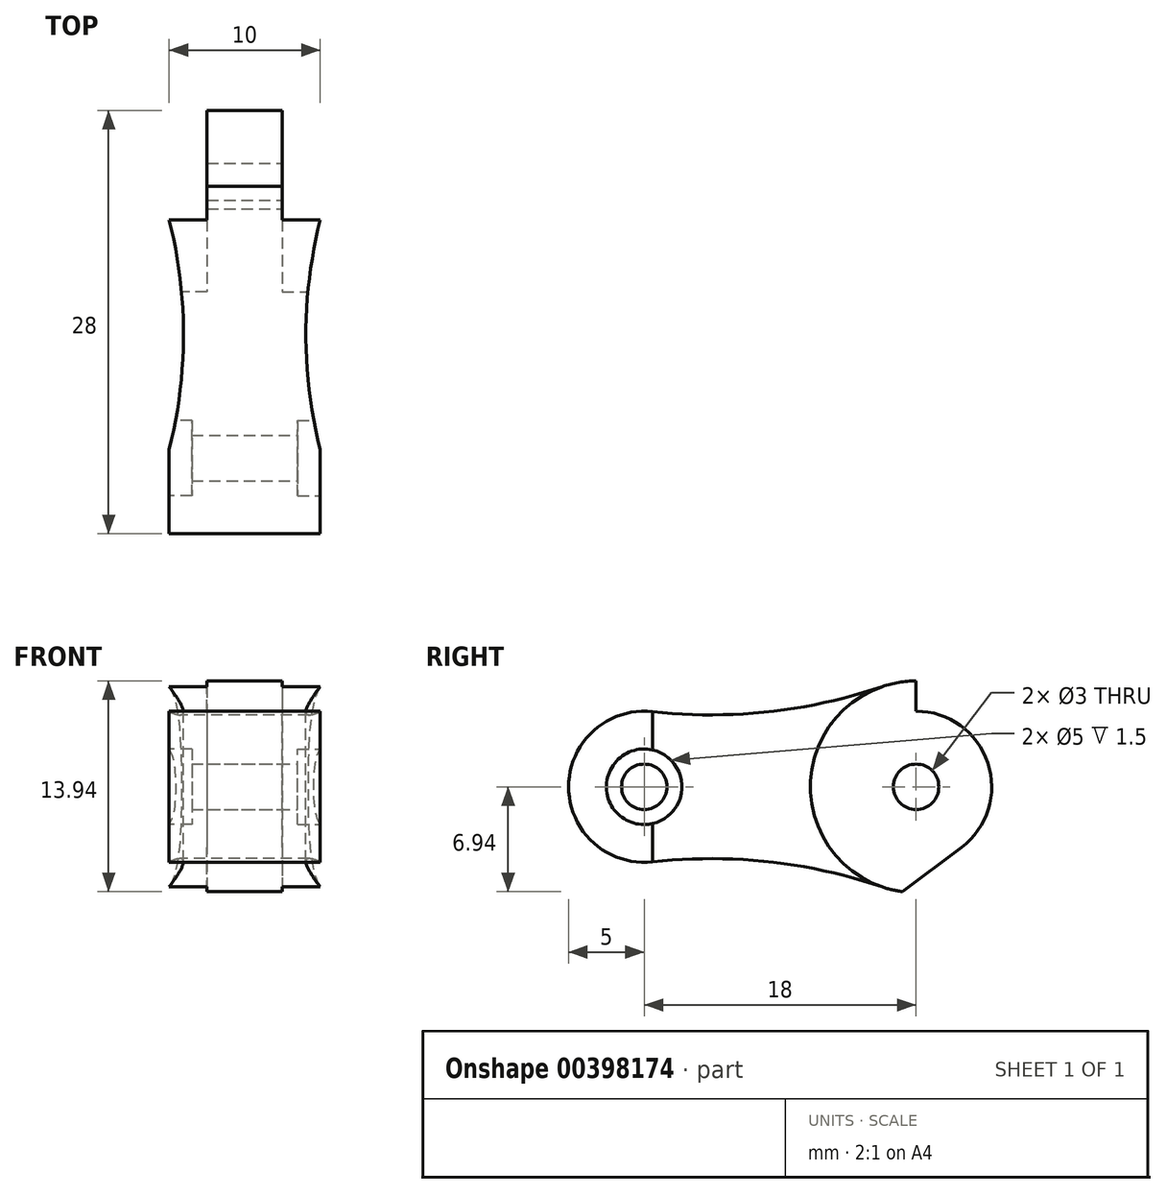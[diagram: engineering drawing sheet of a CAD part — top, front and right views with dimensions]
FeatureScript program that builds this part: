
annotation { "Feature Type Name" : "Feature", "Feature Type Description" : "" }
export const myFeature = defineFeature(function(context is Context, id is Id, definition is map)
    precondition{}
    {
        {
            var Q0;
            Q0=qCreatedBy(makeId("Right.planeOp"),FACE);
            var sketch = newSketch(context, id + "F0", { "sketchPlane" : qUnion([Q0])});
            skArc(sketch, "E0", {"start": v(0.55, 4.97) * mm, "mid": v(-5, 0) * mm, "end": v(0.55, -4.97) * mm});
            skLineSegment(sketch, "E1", {"start": v(-29.92, 0) * mm, "end": v(87.26, 0) * mm, "construction": true});
            skArc(sketch, "E2", {"start": v(15.75, -6.63) * mm, "mid": v(25, 0) * mm, "end": v(15.75, 6.63) * mm});
            skArc(sketch, "E3", {"start": v(0.55, 4.97) * mm, "mid": v(8.24, 4.96) * mm, "end": v(15.75, 6.63) * mm});
            skArc(sketch, "E4", {"start": v(15.75, -6.63) * mm, "mid": v(8.24, -4.96) * mm, "end": v(0.55, -4.97) * mm});
            skSolve(sketch);
        }
        {
            var Q0;
            Q0=qSketchRegion(id+"F0",true);
            extrude(context, id + "F1", {"entities" : qUnion([Q0]), "depth" : 2.5 * mm});
        }
        {
            var Q0;
            Q0=makeQuery(id+"F1.opExtrude","CAP_FACE",FACE,{"disambiguationData":[OSD([sQuery(id+"F0.wireOp",EDGE,"E0"),sQuery(id+"F0.wireOp",EDGE,"E2"),sQuery(id+"F0.wireOp",EDGE,"E3"),sQuery(id+"F0.wireOp",EDGE,"E4")])],"isStart":false});
            var sketch = newSketch(context, id + "F2", { "sketchPlane" : qUnion([Q0])});
            skArc(sketch, "E5.0", {"start": v(0.55, 4.97) * mm, "mid": v(8.24, 4.96) * mm, "end": v(15.75, 6.63) * mm});
            skArc(sketch, "E6.0", {"start": v(15.75, -6.63) * mm, "mid": v(25, 0) * mm, "end": v(15.75, 6.63) * mm});
            skLineSegment(sketch, "E7", {"start": v(0, 0) * mm, "end": v(34.92, 0) * mm, "construction": true});
            skPoint(sketch, "E8.orphan", {"position": v(0.55, -4.97) * mm});
            skArc(sketch, "E9.0", {"start": v(0.55, 4.97) * mm, "mid": v(-5, 0) * mm, "end": v(0.55, -4.97) * mm});
            skArc(sketch, "E10.0", {"start": v(15.75, -6.63) * mm, "mid": v(8.24, -4.96) * mm, "end": v(0.55, -4.97) * mm});
            skSolve(sketch);
        }
        {
            var Q0;
            Q0=qSketchRegion(id+"F2",true);
            extrude(context, id + "F3", {"entities" : qUnion([Q0]), "operationType" : NewBodyOperationType.ADD, "depth" : 5 * mm});
        }
        {
            var Q0;
            Q0=makeQuery(id+"F3.opExtrude","CAP_FACE",FACE,{"disambiguationData":[OSD([sQuery(id+"F2.wireOp",EDGE,"E5.0"),sQuery(id+"F2.wireOp",EDGE,"bc38228c-ca1f-41e0-8e1d-5deb207440e8.0"),sQuery(id+"F2.wireOp",EDGE,"a1095cbb-552a-4b33-82fb-9fb0068e6b7f.0"),sQuery(id+"F2.wireOp",EDGE,"E6.0"),sQuery(id+"F2.wireOp",EDGE,"kkhRfJHV-auDH-NZtS-KPEK-8B2iLmtzf0xF"),sQuery(id+"F2.wireOp",EDGE,"MWx028tx-hoiO-j3L1-AWWv-dpKiWbue3HpV"),sQuery(id+"F2.wireOp",EDGE,"JRJ70NO1-7vJe-Li3z-EIXT-plhISmGAnEbH")])],"isStart":false});
            var sketch = newSketch(context, id + "F4", { "sketchPlane" : qUnion([Q0])});
            skArc(sketch, "E11.0", {"start": v(0.55, 4.97) * mm, "mid": v(8.24, 4.96) * mm, "end": v(15.75, 6.63) * mm});
            skArc(sketch, "E12.0", {"start": v(24.57, -2.42) * mm, "mid": v(23.01, 4.89) * mm, "end": v(15.75, 6.63) * mm});
            skArc(sketch, "E13.0", {"start": v(15.75, -6.63) * mm, "mid": v(25, 0) * mm, "end": v(15.75, 6.63) * mm});
            skArc(sketch, "E14.0", {"start": v(0.55, 4.97) * mm, "mid": v(-5, 0) * mm, "end": v(0.55, -4.97) * mm});
            skArc(sketch, "E15.0", {"start": v(15.75, -6.63) * mm, "mid": v(8.24, -4.96) * mm, "end": v(0.55, -4.97) * mm});
            skSolve(sketch);
        }
        {
            var Q0;
            Q0=qSketchRegion(id+"F4",true);
            extrude(context, id + "F5", {"entities" : qUnion([Q0]), "operationType" : NewBodyOperationType.ADD, "depth" : 2.5 * mm});
        }
        {
            var Q0;
            Q0=makeQuery(id+"F5.opExtrude","CAP_FACE",FACE,{"disambiguationData":[OSD([sQuery(id+"F4.wireOp",EDGE,"b5f4364b-fbc1-4a31-856a-9d50cbaf00ff.0"),sQuery(id+"F4.wireOp",EDGE,"E11.0"),sQuery(id+"F4.wireOp",EDGE,"e0418f54-8eee-4f44-a8f3-dbf9244a5c95.0"),sQuery(id+"F4.wireOp",EDGE,"98b7fe89-a05e-4f80-a394-89aa36924708.0"),sQuery(id+"F4.wireOp",EDGE,"E12.0"),sQuery(id+"F4.wireOp",EDGE,"9f62abc7-1666-4e20-9411-6d2521d5bc1d.0")])],"isStart":false});
            var sketch = newSketch(context, id + "F6", { "sketchPlane" : qUnion([Q0])});
            skCircle(sketch, "E16", {"center": v(18, 0) * mm, "radius": 7 * mm});
            skSolve(sketch);
        }
        {
            var Q0;
            Q0=qSketchRegion(id+"F6",true);
            extrude(context, id + "F7", {"entities" : qUnion([Q0]), "operationType" : NewBodyOperationType.REMOVE, "oppositeDirection" : true, "depth" : 2.5 * mm});
        }
        {
            var Q0;
            Q0=makeQuery(id+"F1.opExtrude","CAP_FACE",FACE,{"disambiguationData":[OSD([sQuery(id+"F0.wireOp",EDGE,"E0"),sQuery(id+"F0.wireOp",EDGE,"E2"),sQuery(id+"F0.wireOp",EDGE,"E3"),sQuery(id+"F0.wireOp",EDGE,"E4")])],"isStart":true});
            var sketch = newSketch(context, id + "F8", { "sketchPlane" : qUnion([Q0])});
            skCircle(sketch, "E17", {"center": v(-18, 0) * mm, "radius": 7 * mm});
            skSolve(sketch);
        }
        {
            var Q0;
            Q0=qSketchRegion(id+"F8",true);
            extrude(context, id + "F9", {"entities" : qUnion([Q0]), "operationType" : NewBodyOperationType.REMOVE, "oppositeDirection" : true, "depth" : 2.5 * mm});
        }
        {
            var Q0;
            Q0=makeQuery(id+"F7.boolean.opBoolean","COPY",FACE,{"derivedFrom":makeQuery(id+"F7.opExtrude","CAP_FACE",FACE,{"disambiguationData":[OSD([sQuery(id+"F6.wireOp",EDGE,"E16")])],"isStart":false})});
            var sketch = newSketch(context, id + "F10", { "sketchPlane" : qUnion([Q0])});
            skArc(sketch, "E18", {"start": v(21, -4) * mm, "mid": v(22.74, 1.58) * mm, "end": v(18, 5) * mm});
            skLineSegment(sketch, "E19", {"start": v(18, 7) * mm, "end": v(18, 5) * mm});
            skArc(sketch, "E20", {"start": v(17.08, -6.94) * mm, "mid": v(24.98, -0.46) * mm, "end": v(18, 7) * mm});
            skLineSegment(sketch, "E21", {"start": v(21, -4) * mm, "end": v(17.08, -6.94) * mm});
            skSolve(sketch);
        }
        {
            var Q0;
            Q0=qSketchRegion(id+"F10",true);
            extrude(context, id + "F11", {"entities" : qUnion([Q0]), "operationType" : NewBodyOperationType.REMOVE, "endBound" : BoundingType.THROUGH_ALL, "oppositeDirection" : true, "depth" : 25 * mm});
        }
        {
            var Q0;
            Q0=makeQuery(id+"F5.opExtrude","CAP_FACE",FACE,{"disambiguationData":[OSD([sQuery(id+"F4.wireOp",EDGE,"b5f4364b-fbc1-4a31-856a-9d50cbaf00ff.0"),sQuery(id+"F4.wireOp",EDGE,"E11.0"),sQuery(id+"F4.wireOp",EDGE,"e0418f54-8eee-4f44-a8f3-dbf9244a5c95.0"),sQuery(id+"F4.wireOp",EDGE,"E12.0"),sQuery(id+"F4.wireOp",EDGE,"9f62abc7-1666-4e20-9411-6d2521d5bc1d.0"),sQuery(id+"F4.wireOp",EDGE,"e2e0c06b-e312-4c98-9337-a9e4e4e6bb38.0")])],"isStart":false});
            var sketch = newSketch(context, id + "F12", { "sketchPlane" : qUnion([Q0])});
            skCircle(sketch, "E22", {"center": v(0, 0) * mm, "radius": 1.5 * mm});
            skCircle(sketch, "E23", {"center": v(18, 0) * mm, "radius": 1.5 * mm});
            skSolve(sketch);
        }
        {
            var Q0;
            Q0=qSketchRegion(id+"F12",true);
            extrude(context, id + "F13", {"entities" : qUnion([Q0]), "operationType" : NewBodyOperationType.REMOVE, "endBound" : BoundingType.THROUGH_ALL, "oppositeDirection" : true, "depth" : 25 * mm});
        }
        {
            var Q0;
            Q0=makeQuery(id+"F5.opExtrude","CAP_FACE",FACE,{"disambiguationData":[OSD([sQuery(id+"F4.wireOp",EDGE,"b5f4364b-fbc1-4a31-856a-9d50cbaf00ff.0"),sQuery(id+"F4.wireOp",EDGE,"E11.0"),sQuery(id+"F4.wireOp",EDGE,"e0418f54-8eee-4f44-a8f3-dbf9244a5c95.0"),sQuery(id+"F4.wireOp",EDGE,"E12.0"),sQuery(id+"F4.wireOp",EDGE,"9f62abc7-1666-4e20-9411-6d2521d5bc1d.0"),sQuery(id+"F4.wireOp",EDGE,"e2e0c06b-e312-4c98-9337-a9e4e4e6bb38.0")])],"isStart":false});
            var sketch = newSketch(context, id + "F14", { "sketchPlane" : qUnion([Q0])});
            skCircle(sketch, "E24", {"center": v(0, 0) * mm, "radius": 2.5 * mm});
            skSolve(sketch);
        }
        {
            var Q0;
            Q0=qSketchRegion(id+"F14",true);
            extrude(context, id + "F15", {"entities" : qUnion([Q0]), "operationType" : NewBodyOperationType.REMOVE, "oppositeDirection" : true, "depth" : 1.5 * mm});
        }
        {
            var Q0;
            Q0=makeQuery(id+"F1.opExtrude","CAP_FACE",FACE,{"disambiguationData":[OSD([sQuery(id+"F0.wireOp",EDGE,"E0"),sQuery(id+"F0.wireOp",EDGE,"E2"),sQuery(id+"F0.wireOp",EDGE,"E3"),sQuery(id+"F0.wireOp",EDGE,"E4")])],"isStart":true});
            var sketch = newSketch(context, id + "F16", { "sketchPlane" : qUnion([Q0])});
            skCircle(sketch, "E25", {"center": v(0, 0) * mm, "radius": 2.5 * mm});
            skSolve(sketch);
        }
        {
            var Q0;
            Q0=qSketchRegion(id+"F16",true);
            extrude(context, id + "F17", {"entities" : qUnion([Q0]), "operationType" : NewBodyOperationType.REMOVE, "oppositeDirection" : true, "depth" : 1.5 * mm});
        }
        {
            var Q0;
            Q0=qCreatedBy(makeId("Top.planeOp"),FACE);
            var sketch = newSketch(context, id + "F18", { "sketchPlane" : qUnion([Q0])});
            skCircle(sketch, "E26", {"center": v(-30, 8.15) * mm, "radius": 30.95 * mm});
            skCircle(sketch, "E27", {"center": v(40, 8.15) * mm, "radius": 30.95 * mm});
            skSolve(sketch);
        }
        {
            var Q0;
            Q0=qSketchRegion(id+"F18",true);
            extrude(context, id + "F19", {"entities" : qUnion([Q0]), "operationType" : NewBodyOperationType.REMOVE, "endBound" : BoundingType.SYMMETRIC, "oppositeDirection" : true, "depth" : 25 * mm});
        }
    });
